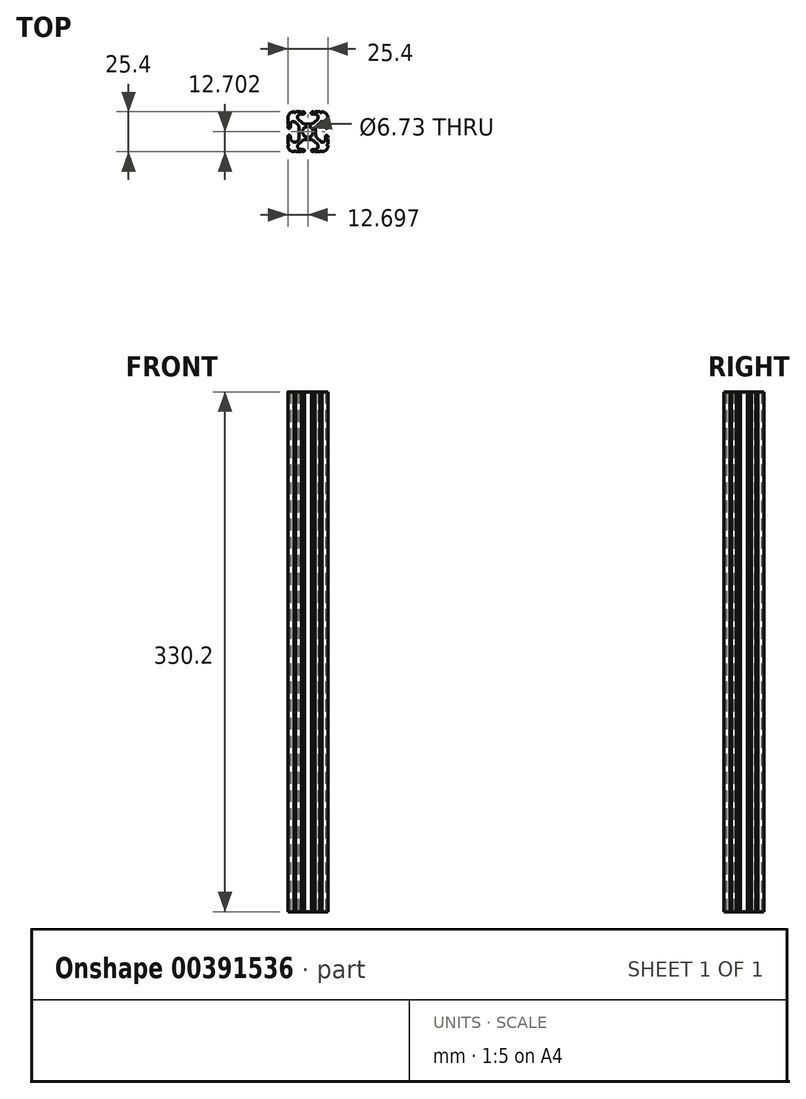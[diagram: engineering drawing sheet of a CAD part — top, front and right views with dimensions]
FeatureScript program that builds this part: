
annotation { "Feature Type Name" : "Feature", "Feature Type Description" : "" }
export const myFeature = defineFeature(function(context is Context, id is Id, definition is map)
    precondition{}
    {
        {
            var Q0;
            Q0=qCreatedBy(makeId("Top.planeOp"),FACE);
            var sketch = newSketch(context, id + "F0", { "sketchPlane" : qUnion([Q0])});
            skCircle(sketch, "E0", {"center": v(-11.44, 9.32) * mm, "radius": 3.36 * mm});
            skLineSegment(sketch, "E1.bottom", {"start": v(-9.99, 14.26) * mm, "end": v(-12.9, 14.26) * mm});
            skLineSegment(sketch, "E1.top", {"start": v(-9.99, 4.38) * mm, "end": v(-12.9, 4.38) * mm});
            skLineSegment(sketch, "E1.left", {"start": v(-6.5, 10.78) * mm, "end": v(-6.5, 7.86) * mm});
            skLineSegment(sketch, "E1.right", {"start": v(-16.98, 11.37) * mm, "end": v(-16.98, 5.6) * mm});
            skPoint(sketch, "E2.visualSharp", {"position": v(-24.14, 22.02) * mm});
            skPoint(sketch, "E3.visualSharp", {"position": v(1.26, 22.02) * mm});
            skPoint(sketch, "E4.visualSharp", {"position": v(1.26, -3.38) * mm});
            skPoint(sketch, "E5.visualSharp", {"position": v(-24.14, -3.38) * mm});
            skLineSegment(sketch, "E6.0", {"start": v(-17.44, 17.22) * mm, "end": v(-15.6, 15.38) * mm});
            skLineSegment(sketch, "E7.0", {"start": v(-19.34, 15.32) * mm, "end": v(-18.1, 14.07) * mm});
            skPoint(sketch, "E8.orphan", {"position": v(-22.6, -1.83) * mm});
            skPoint(sketch, "E9.orphan", {"position": v(-22.6, 20.47) * mm});
            skPoint(sketch, "E10.orphan", {"position": v(-0.3, 20.47) * mm});
            skPoint(sketch, "E11.orphan", {"position": v(-0.3, -1.83) * mm});
            skLineSegment(sketch, "E12", {"start": v(-7.3, 3.27) * mm, "end": v(-5.45, 1.42) * mm});
            skLineSegment(sketch, "E13.0", {"start": v(-17.44, 1.42) * mm, "end": v(-15.6, 3.27) * mm});
            skLineSegment(sketch, "E14.0", {"start": v(-7.3, 15.38) * mm, "end": v(-5.45, 17.22) * mm});
            skPoint(sketch, "E15.visualSharp", {"position": v(-22.6, 18.57) * mm});
            skArc(sketch, "E15.filletArc", {"start": v(-19.34, 15.32) * mm, "mid": v(-21.42, 15.73) * mm, "end": v(-22.6, 13.97) * mm});
            skPoint(sketch, "E16.visualSharp", {"position": v(-20.7, 20.47) * mm});
            skArc(sketch, "E16.filletArc", {"start": v(-16.1, 20.47) * mm, "mid": v(-17.85, 19.3) * mm, "end": v(-17.44, 17.22) * mm});
            skPoint(sketch, "E17.visualSharp", {"position": v(-4.09, 20.47) * mm});
            skLineSegment(sketch, "E18", {"start": v(-16.1, 20.47) * mm, "end": v(-14.33, 20.47) * mm});
            skLineSegment(sketch, "E19", {"start": v(-22.6, 13.97) * mm, "end": v(-22.6, 12.24) * mm});
            skLineSegment(sketch, "E20", {"start": v(-6.8, -1.83) * mm, "end": v(-8.53, -1.83) * mm});
            skArc(sketch, "E21.filletArc", {"start": v(-5.45, 17.22) * mm, "mid": v(-5.03, 19.3) * mm, "end": v(-6.8, 20.47) * mm});
            skPoint(sketch, "E22.visualSharp", {"position": v(-0.3, 0.08) * mm});
            skPoint(sketch, "E23.visualSharp", {"position": v(-2.2, -1.83) * mm});
            skArc(sketch, "E23.filletArc", {"start": v(-6.8, -1.83) * mm, "mid": v(-5.04, -0.65) * mm, "end": v(-5.45, 1.42) * mm});
            skArc(sketch, "E24.filletArc", {"start": v(-17.44, 1.42) * mm, "mid": v(-17.85, -0.65) * mm, "end": v(-16.1, -1.83) * mm});
            skArc(sketch, "E25.filletArc", {"start": v(-22.6, 5.6) * mm, "mid": v(-19.79, 2.8) * mm, "end": v(-16.98, 5.6) * mm});
            skLineSegment(sketch, "E26.bottom", {"start": v(-3.64, -3.38) * mm, "end": v(-6.8, -3.38) * mm});
            skLineSegment(sketch, "E26.top", {"start": v(-3.66, 22.02) * mm, "end": v(-6.8, 22.02) * mm});
            skLineSegment(sketch, "E26.left", {"start": v(1.26, 1.52) * mm, "end": v(1.26, 4.67) * mm});
            skArc(sketch, "E27.filletArc", {"start": v(-24.14, 0.43) * mm, "mid": v(-23.03, -2.26) * mm, "end": v(-20.33, -3.38) * mm});
            skArc(sketch, "E28.filletArc", {"start": v(-2.55, -3.38) * mm, "mid": v(0.14, -2.26) * mm, "end": v(1.26, 0.43) * mm});
            skArc(sketch, "E29.filletArc", {"start": v(1.26, 18.21) * mm, "mid": v(0.14, 20.9) * mm, "end": v(-2.55, 22.02) * mm});
            skArc(sketch, "E30.filletArc", {"start": v(-20.33, 22.02) * mm, "mid": v(-23.03, 20.9) * mm, "end": v(-24.14, 18.21) * mm});
            skPoint(sketch, "E31.newPointA", {"position": v(-16.38, 4.38) * mm});
            skArc(sketch, "E31.filletArc", {"start": v(-12.9, 4.38) * mm, "mid": v(-14.36, 4.1) * mm, "end": v(-15.6, 3.27) * mm});
            skPoint(sketch, "E32.newPointA", {"position": v(-6.5, 4.38) * mm});
            skArc(sketch, "E32.filletArc", {"start": v(-7.3, 3.27) * mm, "mid": v(-8.53, 4.1) * mm, "end": v(-9.99, 4.38) * mm});
            skArc(sketch, "E33.filletArc", {"start": v(-6.5, 7.86) * mm, "mid": v(-6.21, 6.4) * mm, "end": v(-5.39, 5.17) * mm});
            skArc(sketch, "E34.filletArc", {"start": v(-5.39, 13.47) * mm, "mid": v(-6.21, 12.24) * mm, "end": v(-6.5, 10.78) * mm});
            skPoint(sketch, "E35.newPointB", {"position": v(-6.5, 14.26) * mm});
            skArc(sketch, "E35.filletArc", {"start": v(-9.99, 14.26) * mm, "mid": v(-8.53, 14.55) * mm, "end": v(-7.3, 15.38) * mm});
            skPoint(sketch, "E36.newPointB", {"position": v(-16.38, 14.26) * mm});
            skArc(sketch, "E36.filletArc", {"start": v(-15.6, 15.38) * mm, "mid": v(-14.36, 14.55) * mm, "end": v(-12.9, 14.26) * mm});
            skArc(sketch, "E37.filletArc", {"start": v(-16.98, 11.37) * mm, "mid": v(-17.27, 12.83) * mm, "end": v(-18.1, 14.07) * mm});
            skLineSegment(sketch, "E38.filletArc", {"start": v(-16.98, 3.06) * mm, "end": v(-16.98, 3.06) * mm});
            skLineSegment(sketch, "E39", {"start": v(-5.39, 5.17) * mm, "end": v(-3.54, 3.33) * mm});
            skPoint(sketch, "E40.visualSharp", {"position": v(-0.3, 18.57) * mm});
            skArc(sketch, "E41.filletArc", {"start": v(-3.54, 3.33) * mm, "mid": v(-1.47, 2.91) * mm, "end": v(-0.3, 4.67) * mm});
            skLineSegment(sketch, "E42", {"start": v(-0.3, 4.67) * mm, "end": v(-0.3, 6.4) * mm});
            skLineSegment(sketch, "E43", {"start": v(-5.39, 13.47) * mm, "end": v(-3.54, 15.32) * mm});
            skArc(sketch, "E44.filletArc", {"start": v(-0.3, 13.97) * mm, "mid": v(-1.47, 15.73) * mm, "end": v(-3.54, 15.32) * mm});
            skArc(sketch, "E45", {"start": v(-22.6, 6.4) * mm, "mid": v(-23.37, 7.18) * mm, "end": v(-24.14, 6.4) * mm});
            skArc(sketch, "E46", {"start": v(-24.14, 12.24) * mm, "mid": v(-23.37, 11.48) * mm, "end": v(-22.6, 12.24) * mm});
            skArc(sketch, "E47", {"start": v(-14.36, 20.47) * mm, "mid": v(-13.57, 21.25) * mm, "end": v(-14.36, 22.02) * mm});
            skArc(sketch, "E48", {"start": v(-8.53, 22.02) * mm, "mid": v(-9.34, 21.25) * mm, "end": v(-8.53, 20.47) * mm});
            skArc(sketch, "E49", {"start": v(-0.3, 12.24) * mm, "mid": v(0.48, 11.5) * mm, "end": v(1.26, 12.24) * mm});
            skArc(sketch, "E50", {"start": v(1.26, 6.4) * mm, "mid": v(0.48, 7.13) * mm, "end": v(-0.3, 6.4) * mm});
            skArc(sketch, "E51", {"start": v(-8.53, -1.83) * mm, "mid": v(-9.14, -2.6) * mm, "end": v(-8.53, -3.38) * mm});
            skArc(sketch, "E52", {"start": v(-14.36, -3.38) * mm, "mid": v(-13.6, -2.6) * mm, "end": v(-14.36, -1.83) * mm});
            skLineSegment(sketch, "E53.trimOffspring", {"start": v(-14.36, -1.83) * mm, "end": v(-16.1, -1.83) * mm});
            skLineSegment(sketch, "E54.trimOffspring", {"start": v(-15.45, -3.38) * mm, "end": v(-19.23, -3.38) * mm});
            skLineSegment(sketch, "E55.trimOffspring", {"start": v(-0.3, 12.24) * mm, "end": v(-0.3, 13.97) * mm});
            skLineSegment(sketch, "E56.trimOffspring", {"start": v(1.26, 12.24) * mm, "end": v(1.26, 12.88) * mm});
            skLineSegment(sketch, "E57.trimOffspring", {"start": v(-22.6, 6.4) * mm, "end": v(-22.6, 5.6) * mm});
            skLineSegment(sketch, "E58.trimOffspring", {"start": v(-24.14, 12.24) * mm, "end": v(-24.14, 12.88) * mm});
            skLineSegment(sketch, "E59.trimOffspring", {"start": v(-8.6, 20.47) * mm, "end": v(-6.8, 20.47) * mm});
            skLineSegment(sketch, "E60.trimOffspring", {"start": v(-14.33, 22.02) * mm, "end": v(-15, 22.02) * mm});
            skPoint(sketch, "E61.start.orphan", {"position": v(-14.36, 14.55) * mm});
            skPoint(sketch, "E62.start.orphan", {"position": v(-8.53, 14.55) * mm});
            skPoint(sketch, "E63.start.orphan", {"position": v(-6.21, 12.24) * mm});
            skPoint(sketch, "E64.start.orphan", {"position": v(-6.21, 6.4) * mm});
            skPoint(sketch, "E65.start.orphan", {"position": v(-17.27, 12.83) * mm});
            skPoint(sketch, "E66.start.orphan", {"position": v(-16.98, 3.06) * mm});
            skPoint(sketch, "E67.start.orphan", {"position": v(-8.53, 4.1) * mm});
            skPoint(sketch, "E68.start.orphan", {"position": v(-14.36, 4.1) * mm});
            skPoint(sketch, "E69.endSnap0", {"position": v(1.26, 15.22) * mm});
            skPoint(sketch, "E70.startSnap0", {"position": v(-0.3, 5.54) * mm});
            skArc(sketch, "E71", {"start": v(-3.66, 22.02) * mm, "mid": v(-3.1, 21.53) * mm, "end": v(-2.55, 22.02) * mm});
            skArc(sketch, "E72", {"start": v(-7.89, 22.02) * mm, "mid": v(-7.34, 21.48) * mm, "end": v(-6.8, 22.02) * mm});
            skArc(sketch, "E73", {"start": v(-16.1, 22.02) * mm, "mid": v(-15.54, 21.48) * mm, "end": v(-15, 22.02) * mm});
            skArc(sketch, "E74", {"start": v(-20.33, 22.02) * mm, "mid": v(-19.78, 21.47) * mm, "end": v(-19.23, 22.02) * mm});
            skLineSegment(sketch, "E75", {"start": v(-24.14, 18.21) * mm, "end": v(-24.14, 17.13) * mm});
            skArc(sketch, "E76", {"start": v(-24.14, 12.88) * mm, "mid": v(-23.59, 13.42) * mm, "end": v(-24.14, 13.97) * mm});
            skArc(sketch, "E77", {"start": v(-24.14, 0.43) * mm, "mid": v(-23.59, 0.98) * mm, "end": v(-24.14, 1.53) * mm});
            skArc(sketch, "E78", {"start": v(-19.23, -3.38) * mm, "mid": v(-19.78, -2.82) * mm, "end": v(-20.33, -3.38) * mm});
            skArc(sketch, "E79", {"start": v(-14.36, -3.38) * mm, "mid": v(-14.9, -2.84) * mm, "end": v(-15.45, -3.38) * mm});
            skArc(sketch, "E80", {"start": v(-6.8, -3.38) * mm, "mid": v(-7.35, -2.83) * mm, "end": v(-7.9, -3.38) * mm});
            skArc(sketch, "E81", {"start": v(-2.55, -3.38) * mm, "mid": v(-3.1, -2.83) * mm, "end": v(-3.64, -3.38) * mm});
            skLineSegment(sketch, "E82.trimOffspring", {"start": v(-16.1, 22.02) * mm, "end": v(-19.23, 22.02) * mm});
            skLineSegment(sketch, "E83.trimOffspring", {"start": v(-24.14, 13.97) * mm, "end": v(-24.14, 18.21) * mm});
            skLineSegment(sketch, "E84.trimOffspring", {"start": v(-24.14, 5.77) * mm, "end": v(-24.14, 6.4) * mm});
            skLineSegment(sketch, "E85.trimOffspring", {"start": v(-7.9, -3.38) * mm, "end": v(-8.53, -3.38) * mm});
            skArc(sketch, "E86", {"start": v(1.26, 1.52) * mm, "mid": v(0.72, 0.98) * mm, "end": v(1.26, 0.43) * mm});
            skArc(sketch, "E87", {"start": v(1.26, 5.77) * mm, "mid": v(0.71, 5.22) * mm, "end": v(1.26, 4.67) * mm});
            skLineSegment(sketch, "E88.trimOffspring", {"start": v(1.26, 5.77) * mm, "end": v(1.26, 6.4) * mm});
            skArc(sketch, "E89", {"start": v(1.26, 18.21) * mm, "mid": v(0.7, 17.66) * mm, "end": v(1.26, 17.12) * mm});
            skArc(sketch, "E90", {"start": v(1.26, 13.97) * mm, "mid": v(0.71, 13.42) * mm, "end": v(1.26, 12.88) * mm});
            skLineSegment(sketch, "E91.trimOffspring", {"start": v(1.26, 13.97) * mm, "end": v(1.26, 17.12) * mm});
            skLineSegment(sketch, "E92.trimOffspring", {"start": v(-7.89, 22.02) * mm, "end": v(-8.6, 22.02) * mm});
            skLineSegment(sketch, "E93", {"start": v(-24.14, 5.77) * mm, "end": v(-24.14, 1.53) * mm});
            skPoint(sketch, "E94.orphan", {"position": v(-23.2, 5.6) * mm});
            skSolve(sketch);
        }
        {
            var Q0;
            Q0 = qSketchRegion(id + "F0", true);
            extrude(context, id + "F1", {"entities" : qUnion([Q0]), "endBound" : BoundingType.SYMMETRIC, "depth" : 330.2 * mm});
        }
    });
